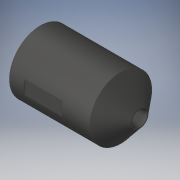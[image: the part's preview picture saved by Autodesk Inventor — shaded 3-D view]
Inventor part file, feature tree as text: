
AUTODESK INVENTOR PART (.ipt)
format: ipt  version: 2018.3 (Build 223285000, 285)  size: 130,048 bytes
history: native  units: mm
features: imported_body x1, thread x1
ambient origin geometry x8: Origin, YZ Plane, XZ Plane, XY Plane, X Axis, Y Axis, Z Axis, Center Point
bodies: Solid1 (feature_tree)
feature tree (2):
  imported_body  "Base1"
  thread  "Thread1"  [1 undecoded]
note: 1 required parameter value undecoded (feature->parameter linkage not recoverable at this tier; creation-order binding heuristic only, values carry confidence <= 0.55)
